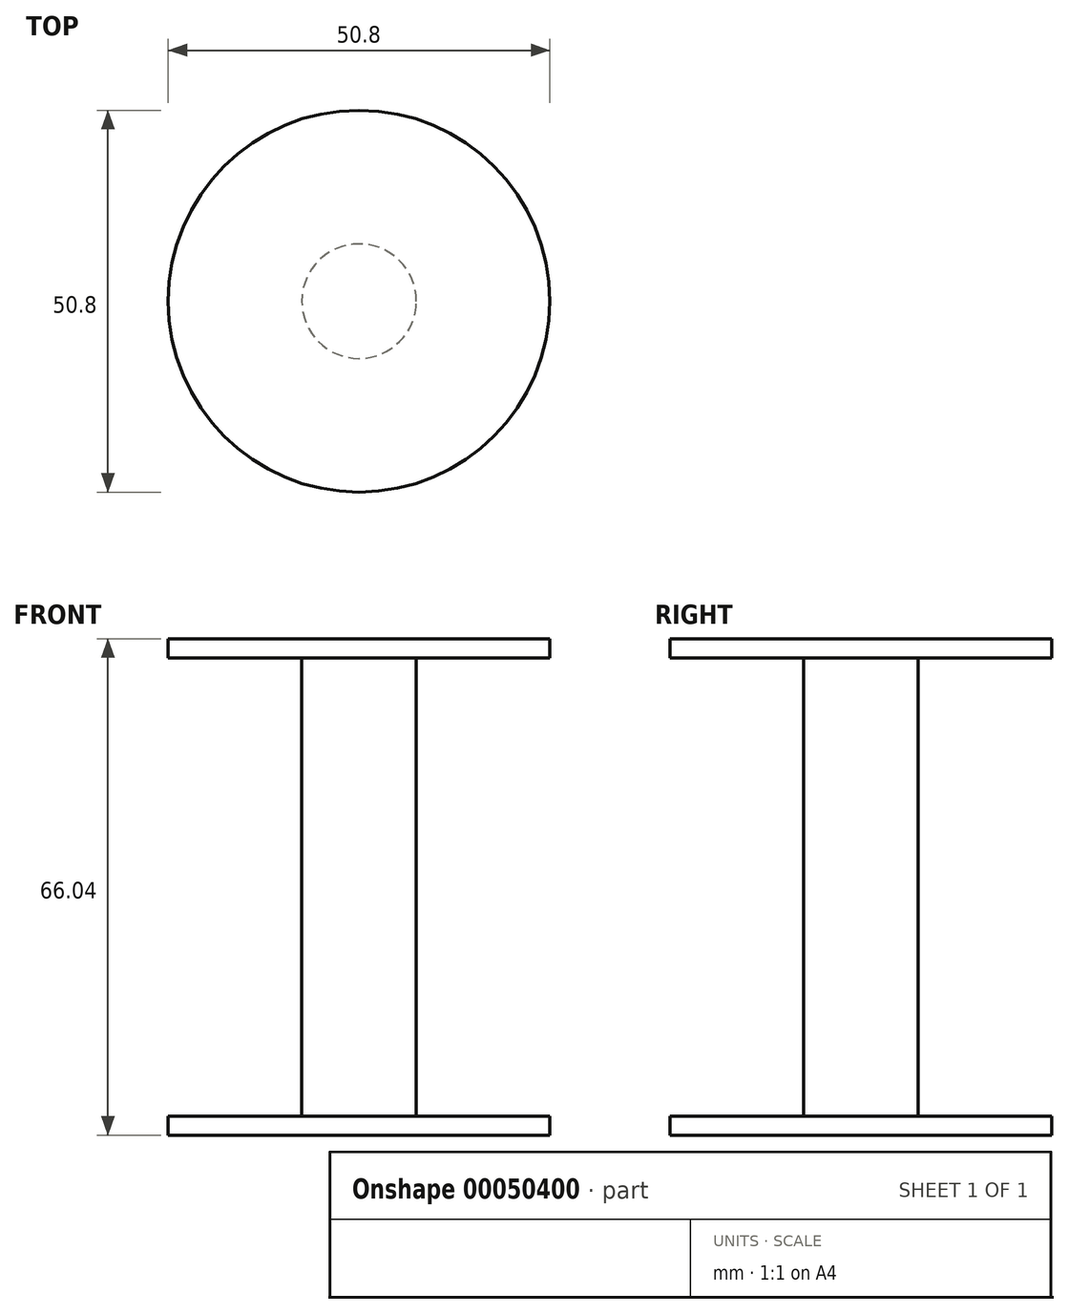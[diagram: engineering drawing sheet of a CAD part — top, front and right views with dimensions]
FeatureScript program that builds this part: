
annotation { "Feature Type Name" : "Feature", "Feature Type Description" : "" }
export const myFeature = defineFeature(function(context is Context, id is Id, definition is map)
    precondition{}
    {
        {
            var Q0;
            Q0=qCreatedBy(makeId("Top.planeOp"),FACE);
            var sketch = newSketch(context, id + "F0", { "sketchPlane" : qUnion([Q0])});
            skCircle(sketch, "E0", {"center": v(0, 0) * mm, "radius": 25.4 * mm});
            skCircle(sketch, "E1", {"center": v(0, 0) * mm, "radius": 7.62 * mm});
            skSolve(sketch);
        }
        {
            var Q0;
            Q0=makeQuery(id+"F0.imprint","IMPRINT",FACE,{"disambiguationData":[TD([[makeQuery(id+"F0.imprint","IMPRINT",EDGE,{"derivedFrom":sQuery(id+"F0.wireOp",EDGE,"E0")}),1.0]])]});
            extrude(context, id + "F1", {"entities" : qUnion([Q0]), "depth" : 2.54 * mm});
        }
        {
            var Q0;
            Q0=makeQuery(id+"F0.imprint","IMPRINT",FACE,{"disambiguationData":[TD([[makeQuery(id+"F0.imprint","IMPRINT",EDGE,{"derivedFrom":sQuery(id+"F0.wireOp",EDGE,"E1")}),1.0]])]});
            extrude(context, id + "F2", {"entities" : qUnion([Q0]), "operationType" : NewBodyOperationType.ADD, "depth" : 63.5 * mm});
        }
        {
            var Q0;
            Q0=makeQuery(id+"F2.opExtrude","CAP_FACE",FACE,{"disambiguationData":[OSD([sQuery(id+"F0.wireOp",EDGE,"E1")])],"isStart":false});
            var sketch = newSketch(context, id + "F3", { "sketchPlane" : qUnion([Q0])});
            skCircle(sketch, "E2", {"center": v(0, 0) * mm, "radius": 25.4 * mm});
            skSolve(sketch);
        }
        {
            var Q0;
            Q0=makeQuery(id+"F3.imprint","IMPRINT",FACE,{"disambiguationData":[TD([[makeQuery(id+"F3.imprint","IMPRINT",EDGE,{"derivedFrom":sQuery(id+"F3.wireOp",EDGE,"E2")}),1.0]])]});
            var Q1;
            Q1=makeQuery(id+"F3.imprint","IMPRINT",FACE,{"disambiguationData":[TD([[makeQuery(id+"F3.imprint","IMPRINT",EDGE,{"derivedFrom":makeQuery(id+"F2.opExtrude","CAP_EDGE",EDGE,{"disambiguationData":[OSD([sQuery(id+"F0.wireOp",EDGE,"E1")])],"isStart":false})}),1.0]])]});
            extrude(context, id + "F4", {"entities" : qUnion([Q0, Q1]), "operationType" : NewBodyOperationType.ADD, "depth" : 2.54 * mm});
        }
    });
